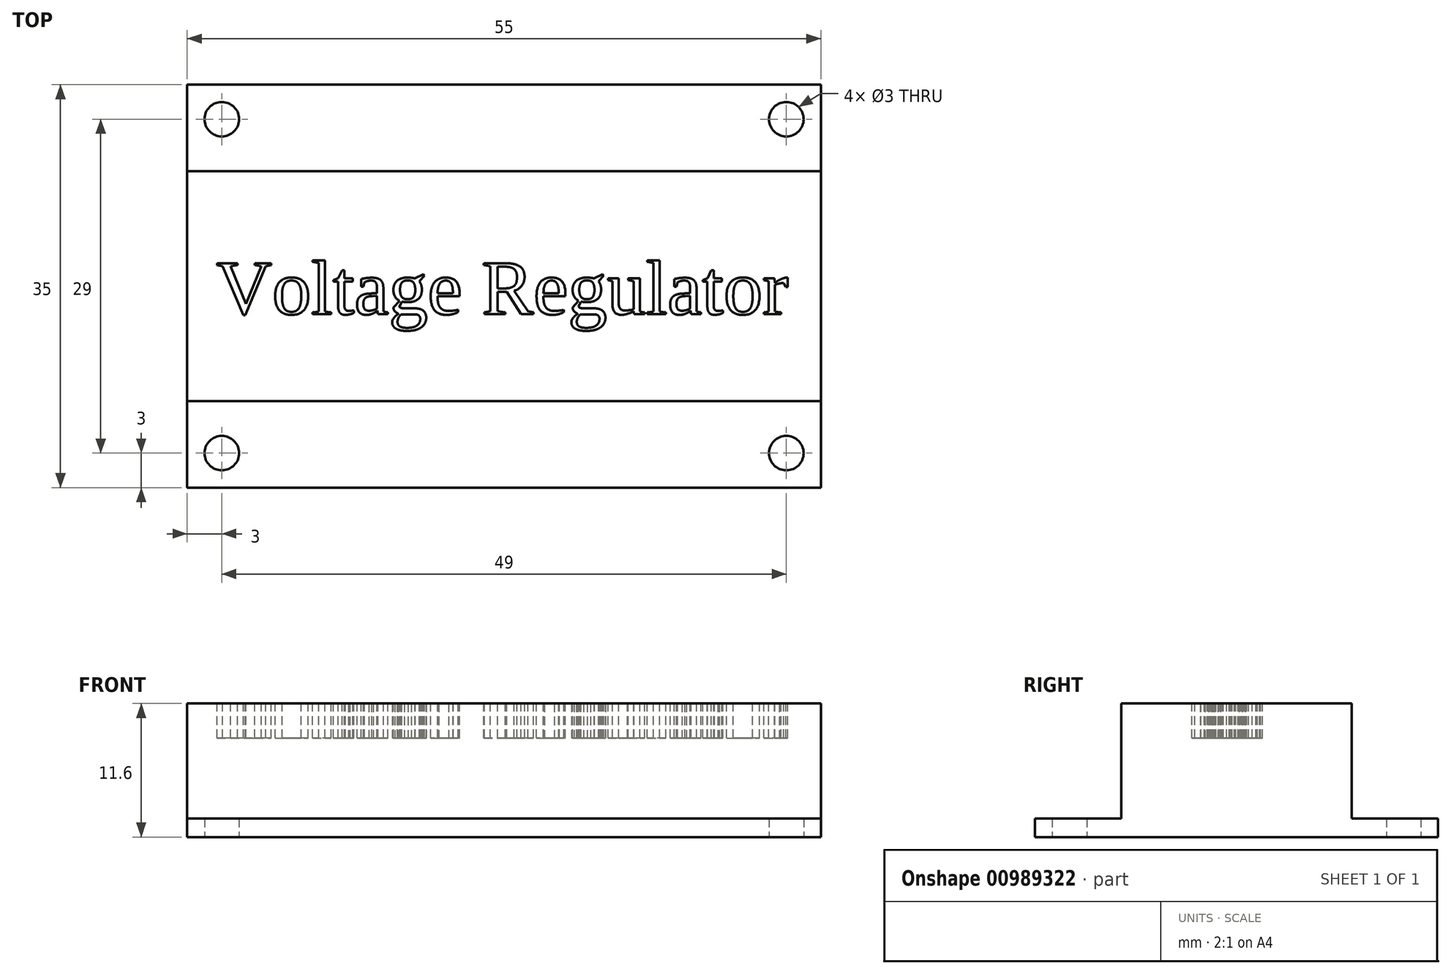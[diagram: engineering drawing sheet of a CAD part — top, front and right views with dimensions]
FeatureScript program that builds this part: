
annotation { "Feature Type Name" : "Feature", "Feature Type Description" : "" }
export const myFeature = defineFeature(function(context is Context, id is Id, definition is map)
    precondition{}
    {
        {
            var Q0;
            Q0=qCreatedBy(makeId("Top.planeOp"),FACE);
            var sketch = newSketch(context, id + "F0", { "sketchPlane" : qUnion([Q0])});
            skLineSegment(sketch, "E0.bottom", {"start": v(27.5, 17.5) * mm, "end": v(-27.5, 17.5) * mm});
            skLineSegment(sketch, "E0.top", {"start": v(27.5, -17.5) * mm, "end": v(-27.5, -17.5) * mm});
            skLineSegment(sketch, "E0.left", {"start": v(27.5, 17.5) * mm, "end": v(27.5, -17.5) * mm});
            skLineSegment(sketch, "E0.right", {"start": v(-27.5, 17.5) * mm, "end": v(-27.5, -17.5) * mm});
            skPoint(sketch, "E0.middle", {"position": v(0, 0) * mm});
            skCircle(sketch, "E1", {"center": v(-24.5, 14.5) * mm, "radius": 1.5 * mm});
            skCircle(sketch, "E2.0.1.0", {"center": v(-24.5, -14.5) * mm, "radius": 1.5 * mm});
            skCircle(sketch, "E2.1.0.0", {"center": v(24.5, 14.5) * mm, "radius": 1.5 * mm});
            skCircle(sketch, "E2.1.1.0", {"center": v(24.5, -14.5) * mm, "radius": 1.5 * mm});
            skLineSegment(sketch, "E2.direction1", {"start": v(-24.5, 14.5) * mm, "end": v(24.5, 14.5) * mm, "construction": true});
            skLineSegment(sketch, "E2.direction2", {"start": v(-24.5, 14.5) * mm, "end": v(-24.5, -14.5) * mm, "construction": true});
            skSolve(sketch);
        }
        {
            var Q0;
            Q0=qSketchRegion(id+"F0",true);
            extrude(context, id + "F1", {"entities" : qUnion([Q0]), "depth" : 1.6 * mm, "offsetDistance" : 25 * mm});
        }
        {
            var Q0;
            Q0=makeQuery(id+"F1.opExtrude","CAP_FACE",FACE,{"disambiguationData":[OSD([sQuery(id+"F0.wireOp",EDGE,"E0.bottom"),sQuery(id+"F0.wireOp",EDGE,"E0.top"),sQuery(id+"F0.wireOp",EDGE,"E0.left"),sQuery(id+"F0.wireOp",EDGE,"E0.right"),sQuery(id+"F0.wireOp",EDGE,"E1"),sQuery(id+"F0.wireOp",EDGE,"E2.0.1.0"),sQuery(id+"F0.wireOp",EDGE,"E2.1.0.0"),sQuery(id+"F0.wireOp",EDGE,"E2.1.1.0")])],"isStart":false});
            var sketch = newSketch(context, id + "F2", { "sketchPlane" : qUnion([Q0])});
            skLineSegment(sketch, "E3.bottom", {"start": v(27.5, 10) * mm, "end": v(-27.5, 10) * mm});
            skLineSegment(sketch, "E3.top", {"start": v(27.5, -10) * mm, "end": v(-27.5, -10) * mm});
            skLineSegment(sketch, "E3.left", {"start": v(27.5, 10) * mm, "end": v(27.5, -10) * mm});
            skLineSegment(sketch, "E3.right", {"start": v(-27.5, 10) * mm, "end": v(-27.5, -10) * mm});
            skPoint(sketch, "E3.middle", {"position": v(0, 0) * mm});
            skSolve(sketch);
        }
        {
            var Q0;
            Q0=qSketchRegion(id+"F2",true);
            extrude(context, id + "F3", {"entities" : qUnion([Q0]), "operationType" : NewBodyOperationType.ADD, "depth" : 10 * mm, "offsetDistance" : 25 * mm});
        }
        {
            var Q0;
            Q0=makeQuery(id+"F3.opExtrude","CAP_FACE",FACE,{"disambiguationData":[OSD([sQuery(id+"F2.wireOp",EDGE,"E3.bottom"),sQuery(id+"F2.wireOp",EDGE,"E3.top"),sQuery(id+"F2.wireOp",EDGE,"E3.left"),sQuery(id+"F2.wireOp",EDGE,"E3.right")])],"isStart":false});
            var sketch = newSketch(context, id + "F4", { "sketchPlane" : qUnion([Q0])});
            skText(sketch, "E4", { "text": "Voltage Regulator", "fontName": "Tinos-Regular.ttf"});
            const initialGuessF4  = {"E4": [-0.025, -0.00243, 1, 0, 0.00486]};
            skSetInitialGuess(sketch, initialGuessF4);
            skSolve(sketch);
        }
        {
            var Q0;
            Q0=qSketchRegion(id+"F4",true);
            extrude(context, id + "F5", {"entities" : qUnion([Q0]), "operationType" : NewBodyOperationType.REMOVE, "oppositeDirection" : true, "depth" : 3 * mm, "offsetDistance" : 25 * mm});
        }
    });
